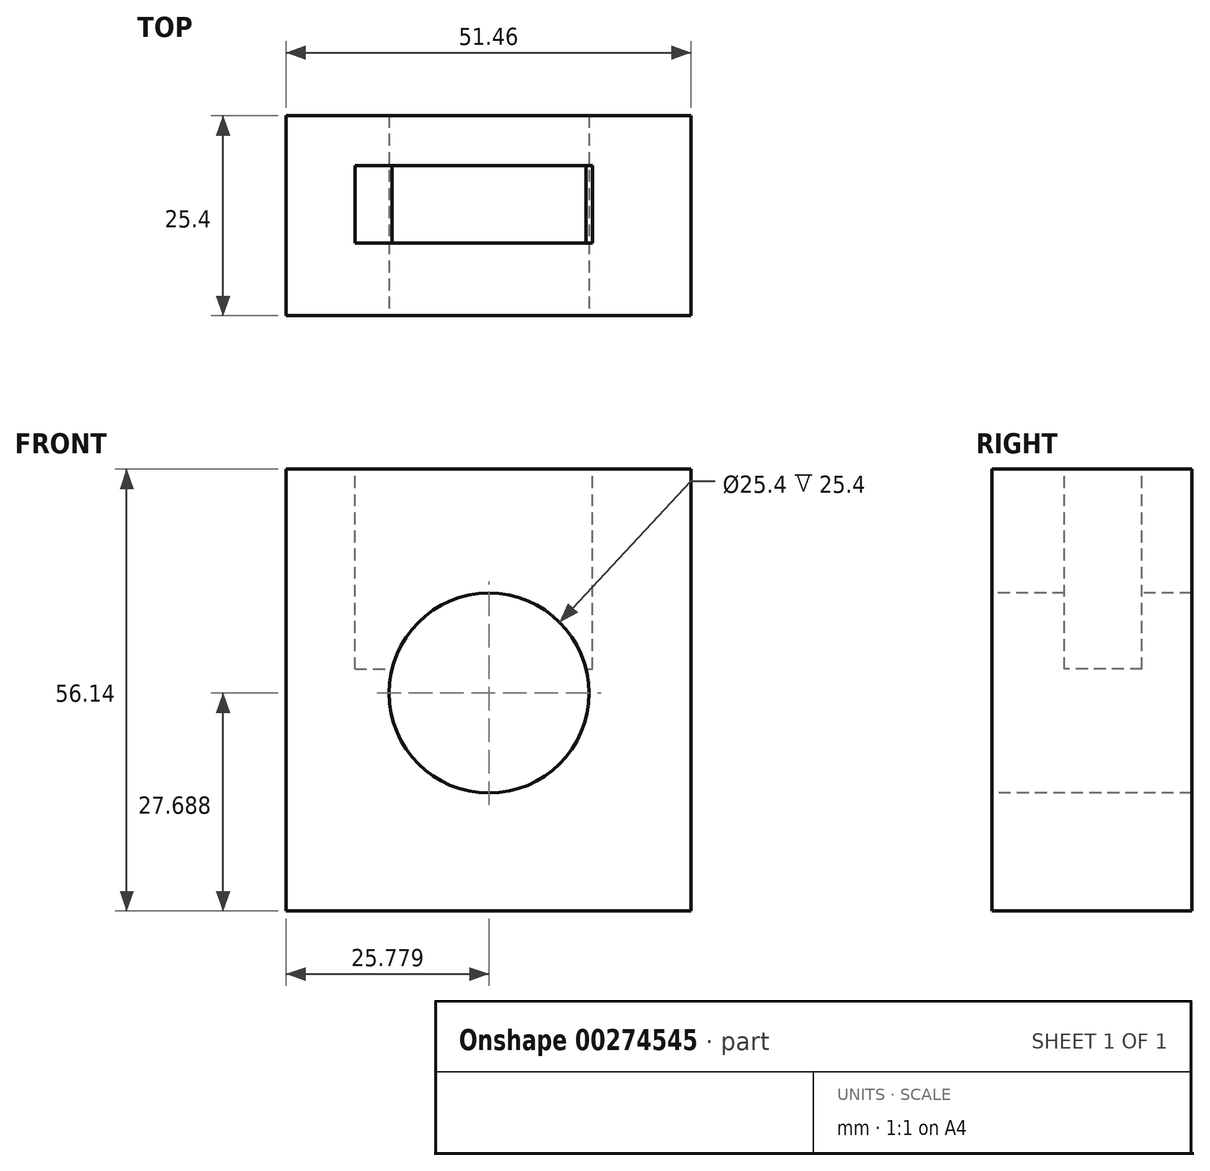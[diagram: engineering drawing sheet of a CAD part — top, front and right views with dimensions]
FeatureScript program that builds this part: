
annotation { "Feature Type Name" : "Feature", "Feature Type Description" : "" }
export const myFeature = defineFeature(function(context is Context, id is Id, definition is map)
    precondition{}
    {
        {
            var Q0;
            Q0=qCreatedBy(makeId("Front.planeOp"),FACE);
            var sketch = newSketch(context, id + "F0", { "sketchPlane" : qUnion([Q0])});
            skLineSegment(sketch, "E0.bottom", {"start": v(0, 0) * mm, "end": v(51.46, 0) * mm});
            skLineSegment(sketch, "E0.top", {"start": v(0, 56.14) * mm, "end": v(51.46, 56.14) * mm});
            skLineSegment(sketch, "E0.left", {"start": v(0, 0) * mm, "end": v(0, 56.14) * mm});
            skLineSegment(sketch, "E0.right", {"start": v(51.46, 0) * mm, "end": v(51.46, 56.14) * mm});
            skSolve(sketch);
        }
        {
            var Q0;
            Q0=makeQuery(id+"F0.imprint","IMPRINT",FACE,{"disambiguationData":[TD([[makeQuery(id+"F0.imprint","IMPRINT",EDGE,{"derivedFrom":sQuery(id+"F0.wireOp",EDGE,"E0.bottom")}),1.0]])]});
            extrude(context, id + "F1", {"entities" : qUnion([Q0]), "depth" : 25.4 * mm});
        }
        {
            var Q0;
            Q0=makeQuery(id+"F1.opExtrude","CAP_FACE",FACE,{"disambiguationData":[OSD([sQuery(id+"F0.wireOp",EDGE,"E0.bottom"),sQuery(id+"F0.wireOp",EDGE,"E0.top"),sQuery(id+"F0.wireOp",EDGE,"E0.left"),sQuery(id+"F0.wireOp",EDGE,"E0.right")])],"isStart":false});
            var sketch = newSketch(context, id + "F2", { "sketchPlane" : qUnion([Q0])});
            skCircle(sketch, "E1", {"center": v(25.78, 27.69) * mm, "radius": 12.7 * mm});
            skSolve(sketch);
        }
        {
            var Q0;
            Q0 = qSketchRegion(id + "F2", true);
            extrude(context, id + "F3", {"entities" : qUnion([Q0]), "operationType" : NewBodyOperationType.REMOVE, "oppositeDirection" : true, "depth" : 25.4 * mm});
        }
        {
            var Q0;
            Q0=makeQuery(id+"F1.opExtrude","SWEPT_FACE",FACE,{"disambiguationData":[OSD([sQuery(id+"F0.wireOp",EDGE,"E0.top")])]});
            var sketch = newSketch(context, id + "F4", { "sketchPlane" : qUnion([Q0])});
            skLineSegment(sketch, "E2.bottom", {"start": v(8.75, -6.31) * mm, "end": v(38.93, -6.31) * mm});
            skLineSegment(sketch, "E2.top", {"start": v(8.75, -16.19) * mm, "end": v(38.93, -16.19) * mm});
            skLineSegment(sketch, "E2.left", {"start": v(8.75, -6.31) * mm, "end": v(8.75, -16.19) * mm});
            skLineSegment(sketch, "E2.right", {"start": v(38.93, -6.31) * mm, "end": v(38.93, -16.19) * mm});
            skSolve(sketch);
        }
        {
            var Q0;
            Q0 = qSketchRegion(id + "F4", true);
            extrude(context, id + "F5", {"entities" : qUnion([Q0]), "operationType" : NewBodyOperationType.REMOVE, "oppositeDirection" : true, "depth" : 25.4 * mm});
        }
    });
